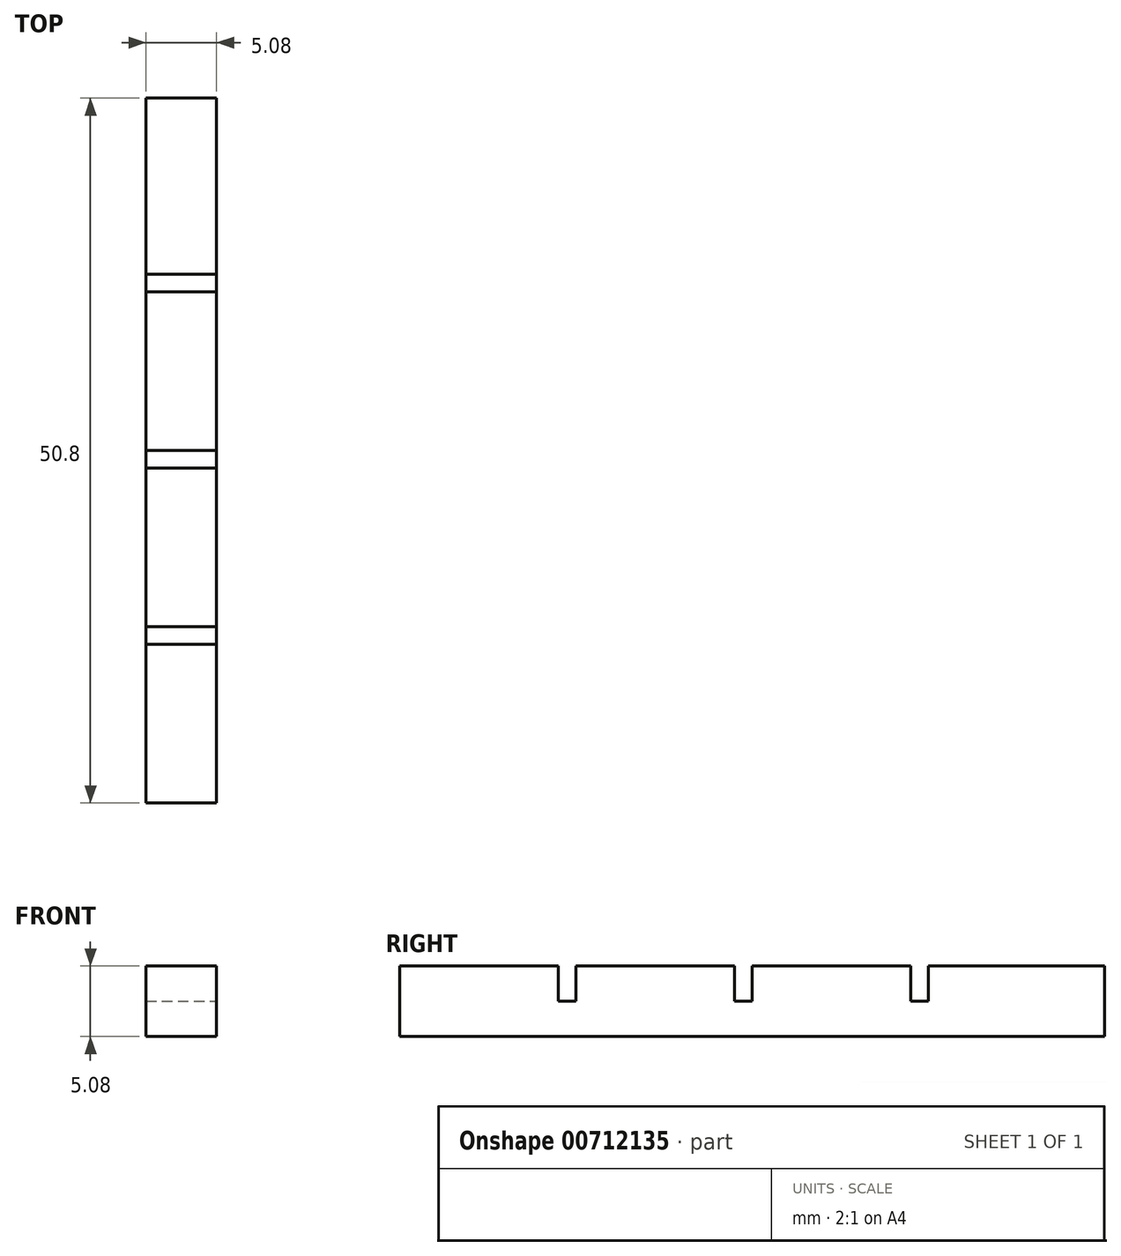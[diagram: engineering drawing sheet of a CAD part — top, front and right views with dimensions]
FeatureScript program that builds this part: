
annotation { "Feature Type Name" : "Feature", "Feature Type Description" : "" }
export const myFeature = defineFeature(function(context is Context, id is Id, definition is map)
    precondition{}
    {
        {
            var Q0;
            Q0=qCreatedBy(makeId("Top.planeOp"),FACE);
            var sketch = newSketch(context, id + "F0", { "sketchPlane" : qUnion([Q0])});
            skLineSegment(sketch, "E0.bottom", {"start": v(-32.56, 16.78) * mm, "end": v(-37.64, 16.78) * mm});
            skLineSegment(sketch, "E0.top", {"start": v(-32.56, 67.58) * mm, "end": v(-37.64, 67.58) * mm});
            skLineSegment(sketch, "E0.left", {"start": v(-32.56, 16.78) * mm, "end": v(-32.56, 67.58) * mm});
            skLineSegment(sketch, "E0.right", {"start": v(-37.64, 16.78) * mm, "end": v(-37.64, 67.58) * mm});
            skPoint(sketch, "E0.middle", {"position": v(-35.1, 42.18) * mm});
            skSolve(sketch);
        }
        {
            var Q0;
            Q0=makeQuery(id+"F0.imprint","IMPRINT",FACE,{"disambiguationData":[TD([[makeQuery(id+"F0.imprint","IMPRINT",EDGE,{"derivedFrom":sQuery(id+"F0.wireOp",EDGE,"E0.bottom")}),-1.0]])]});
            extrude(context, id + "F1", {"entities" : qUnion([Q0]), "depth" : 5.08 * mm, "offsetDistance" : 25.4 * mm});
        }
        {
            var Q0;
            Q0=makeQuery(id+"F1.opExtrude","CAP_FACE",FACE,{"disambiguationData":[OSD([sQuery(id+"F0.wireOp",EDGE,"E0.bottom"),sQuery(id+"F0.wireOp",EDGE,"E0.top"),sQuery(id+"F0.wireOp",EDGE,"E0.left"),sQuery(id+"F0.wireOp",EDGE,"E0.right")])],"isStart":false});
            var sketch = newSketch(context, id + "F2", { "sketchPlane" : qUnion([Q0])});
            skLineSegment(sketch, "E1.bottom", {"start": v(-37.64, 54.88) * mm, "end": v(-32.56, 54.88) * mm});
            skLineSegment(sketch, "E1.top", {"start": v(-37.64, 53.6) * mm, "end": v(-32.56, 53.6) * mm});
            skLineSegment(sketch, "E1.left", {"start": v(-37.64, 54.88) * mm, "end": v(-37.64, 53.6) * mm});
            skLineSegment(sketch, "E1.right", {"start": v(-32.56, 54.88) * mm, "end": v(-32.56, 53.6) * mm});
            skLineSegment(sketch, "E2.bottom", {"start": v(-37.64, 42.18) * mm, "end": v(-32.56, 42.18) * mm});
            skLineSegment(sketch, "E2.top", {"start": v(-37.64, 40.9) * mm, "end": v(-32.56, 40.9) * mm});
            skLineSegment(sketch, "E2.left", {"start": v(-37.64, 42.18) * mm, "end": v(-37.64, 40.9) * mm});
            skLineSegment(sketch, "E2.right", {"start": v(-32.56, 42.18) * mm, "end": v(-32.56, 40.9) * mm});
            skLineSegment(sketch, "E3.bottom", {"start": v(-37.64, 29.48) * mm, "end": v(-32.56, 29.48) * mm});
            skLineSegment(sketch, "E3.top", {"start": v(-37.64, 28.2) * mm, "end": v(-32.56, 28.2) * mm});
            skLineSegment(sketch, "E3.left", {"start": v(-37.64, 29.48) * mm, "end": v(-37.64, 28.2) * mm});
            skLineSegment(sketch, "E3.right", {"start": v(-32.56, 29.48) * mm, "end": v(-32.56, 28.2) * mm});
            skSolve(sketch);
        }
        {
            var Q0;
            Q0=makeQuery(id+"F2.imprint","IMPRINT",FACE,{"disambiguationData":[TD([[makeQuery(id+"F2.imprint","IMPRINT",EDGE,{"derivedFrom":sQuery(id+"F2.wireOp",EDGE,"E1.bottom")}),-1.0]])]});
            var Q1;
            Q1=makeQuery(id+"F2.imprint","IMPRINT",FACE,{"disambiguationData":[TD([[makeQuery(id+"F2.imprint","IMPRINT",EDGE,{"derivedFrom":sQuery(id+"F2.wireOp",EDGE,"E2.bottom")}),-1.0]])]});
            var Q2;
            Q2=makeQuery(id+"F2.imprint","IMPRINT",FACE,{"disambiguationData":[TD([[makeQuery(id+"F2.imprint","IMPRINT",EDGE,{"derivedFrom":sQuery(id+"F2.wireOp",EDGE,"E3.bottom")}),-1.0]])]});
            extrude(context, id + "F3", {"entities" : qUnion([Q0, Q1, Q2]), "operationType" : NewBodyOperationType.REMOVE, "oppositeDirection" : true, "depth" : 2.54 * mm, "offsetDistance" : 25.4 * mm});
        }
    });
